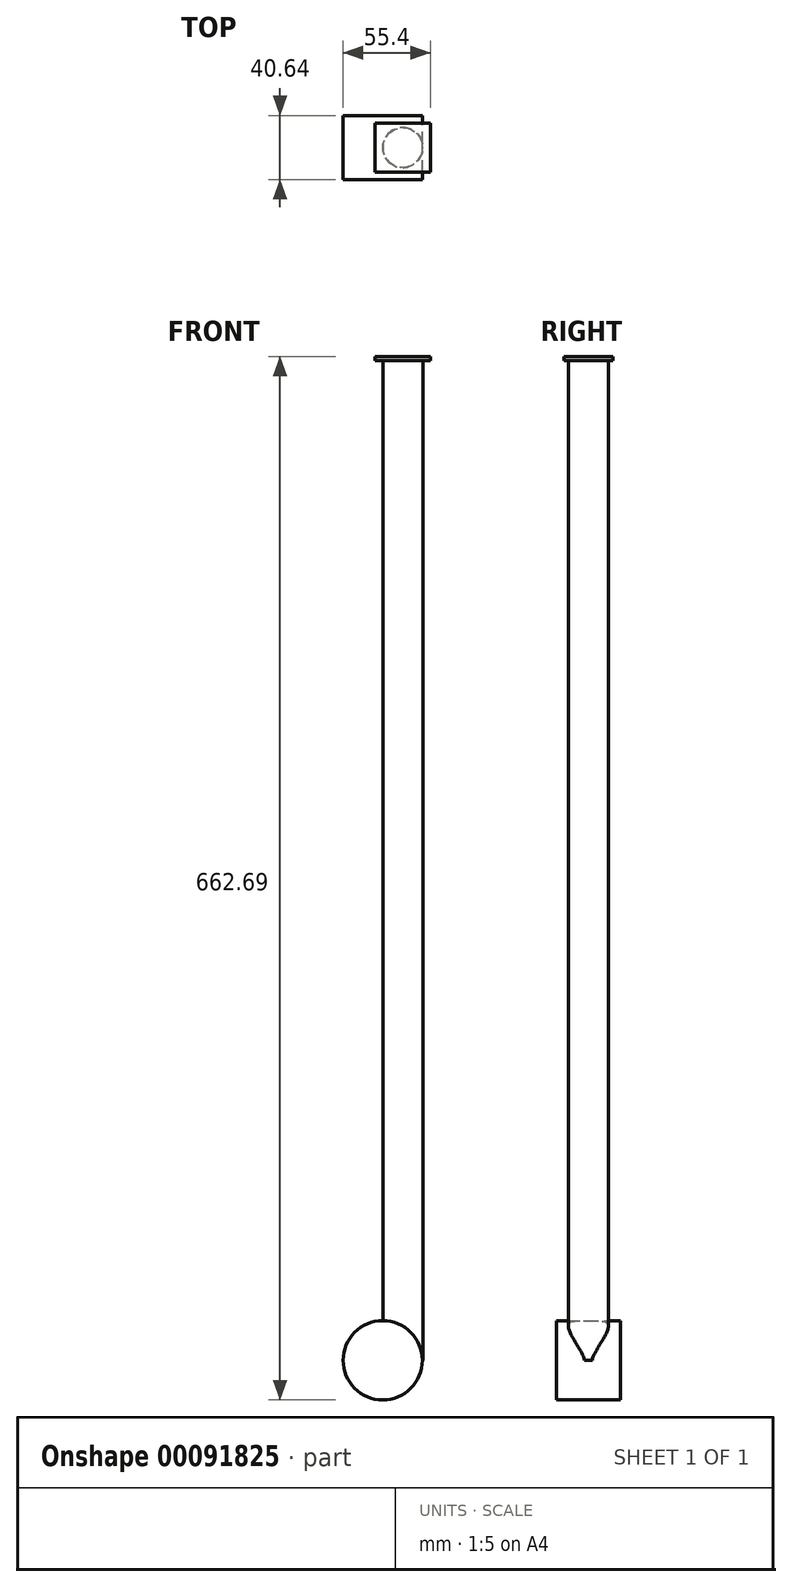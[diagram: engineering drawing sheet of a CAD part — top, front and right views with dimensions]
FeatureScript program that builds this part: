
annotation { "Feature Type Name" : "Feature", "Feature Type Description" : "" }
export const myFeature = defineFeature(function(context is Context, id is Id, definition is map)
    precondition{}
    {
        {
            var Q0;
            Q0=qCreatedBy(makeId("Top.planeOp"),FACE);
            var sketch = newSketch(context, id + "F0", { "sketchPlane" : qUnion([Q0])});
            skCircle(sketch, "E0", {"center": v(0, 0) * mm, "radius": 12.7 * mm});
            skSolve(sketch);
        }
        {
            var Q0;
            Q0=makeQuery(id+"F0.imprint","IMPRINT",FACE,{"disambiguationData":[TD([[makeQuery(id+"F0.imprint","IMPRINT",EDGE,{"derivedFrom":sQuery(id+"F0.wireOp",EDGE,"E0")}),1.0]])]});
            extrude(context, id + "F1", {"entities" : qUnion([Q0]), "depth" : 635 * mm});
        }
        {
            var Q0;
            Q0=qCreatedBy(makeId("Front.planeOp"),FACE);
            var sketch = newSketch(context, id + "F2", { "sketchPlane" : qUnion([Q0])});
            skCircle(sketch, "E1", {"center": v(-12.72, 0) * mm, "radius": 25.15 * mm});
            skSolve(sketch);
        }
        {
            var Q0;
            Q0 = qSketchRegion(id + "F2", true);
            extrude(context, id + "F3", {"entities" : qUnion([Q0]), "operationType" : NewBodyOperationType.ADD, "depth" : 20.32 * mm});
        }
        {
            var Q0;
            Q0=makeQuery(id+"F1.opExtrude","SWEPT_BODY",BODY,{"disambiguationData":[OSD([sQuery(id+"F0.wireOp",EDGE,"E0")])]});
            var Q1;
            Q1=qCreatedBy(makeId("Front.planeOp"),FACE);
            mirror(context, id + "F4", {"operationType" : NewBodyOperationType.ADD, "entities" : qUnion([Q0]), "mirrorPlane" : qUnion([Q1])});
        }
        {
            var Q0;
            Q0=makeQuery(id+"F1.opExtrude","CAP_FACE",FACE,{"disambiguationData":[OSD([sQuery(id+"F0.wireOp",EDGE,"E0")])],"isStart":false});
            var sketch = newSketch(context, id + "F5", { "sketchPlane" : qUnion([Q0])});
            skLineSegment(sketch, "E2.bottom", {"start": v(17.53, 15.61) * mm, "end": v(-17.53, 15.61) * mm});
            skLineSegment(sketch, "E2.top", {"start": v(17.53, -15.61) * mm, "end": v(-17.53, -15.61) * mm});
            skLineSegment(sketch, "E2.left", {"start": v(17.53, 15.61) * mm, "end": v(17.53, -15.61) * mm});
            skLineSegment(sketch, "E2.right", {"start": v(-17.53, 15.61) * mm, "end": v(-17.53, -15.61) * mm});
            skPoint(sketch, "E2.middle", {"position": v(0, 0) * mm});
            skSolve(sketch);
        }
        {
            var Q0;
            Q0 = qSketchRegion(id + "F5", true);
            extrude(context, id + "F6", {"entities" : qUnion([Q0]), "operationType" : NewBodyOperationType.ADD, "depth" : 2.54 * mm});
        }
    });
